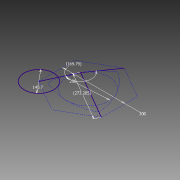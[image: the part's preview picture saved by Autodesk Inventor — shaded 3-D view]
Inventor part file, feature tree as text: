
AUTODESK INVENTOR PART (.ipt)
format: ipt  version: 2013 (Build 170138000, 138)  size: 68,608 bytes
history: native  units: mm
features: sketch x1
ambient origin geometry x8: Origin, YZ Plane, XZ Plane, XY Plane, X Axis, Y Axis, Z Axis, Center Point
feature tree (1):
  sketch  "Sketch1"  dims[d0=300.0mm d4=200.0mm d5=33.197527mm d6=140.7mm d7=273.205081mm]
